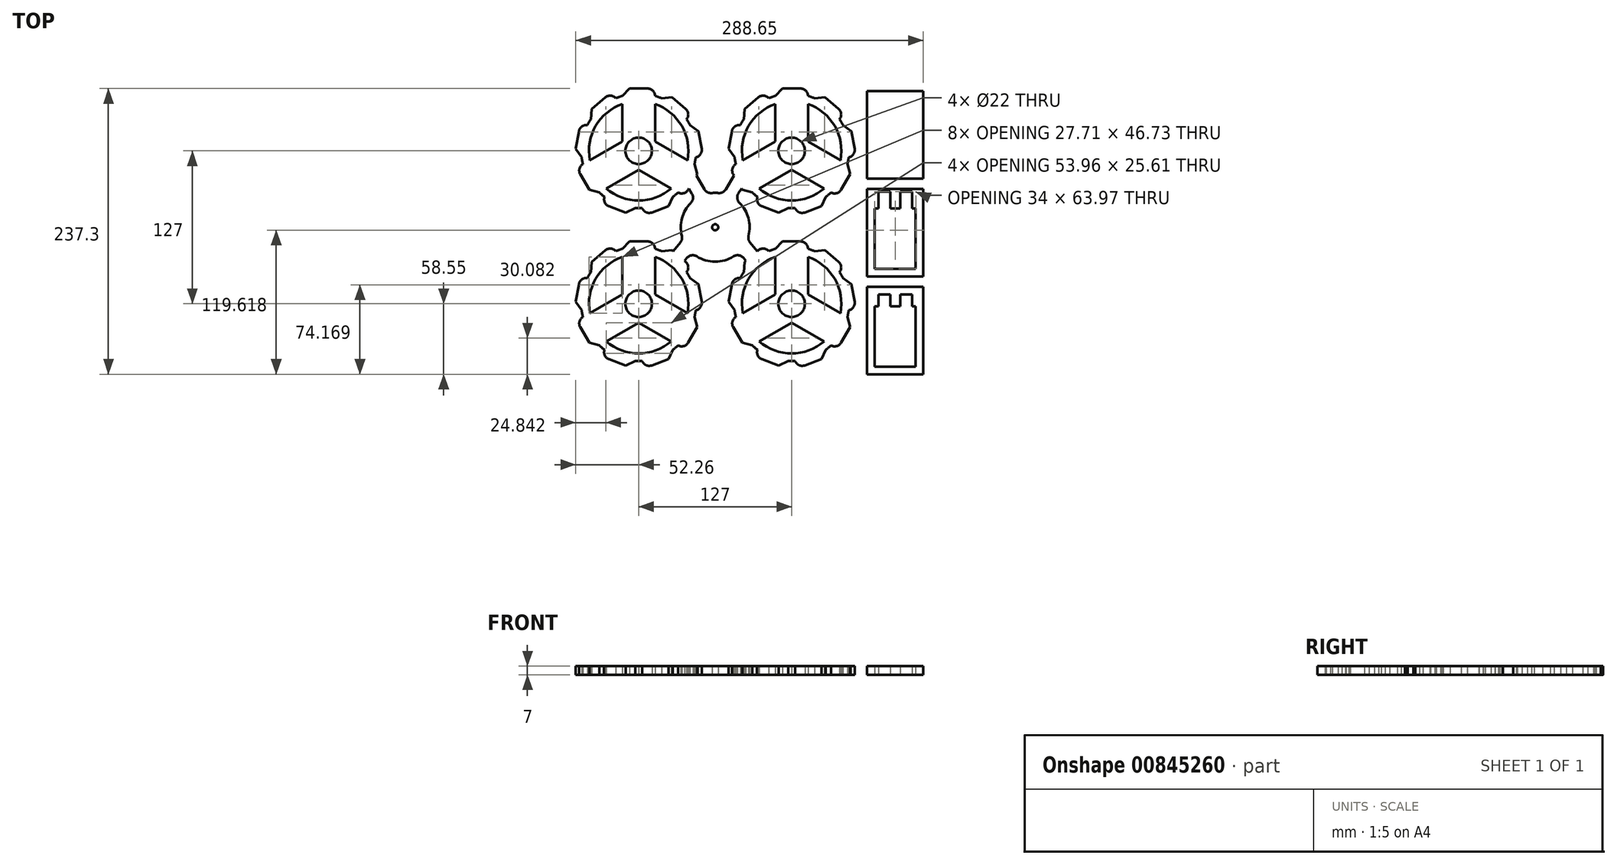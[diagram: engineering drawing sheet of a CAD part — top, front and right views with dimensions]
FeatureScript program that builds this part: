
annotation { "Feature Type Name" : "Feature", "Feature Type Description" : "" }
export const myFeature = defineFeature(function(context is Context, id is Id, definition is map)
    precondition{}
    {
        {
            var Q0;
            Q0=qCreatedBy(makeId("Top.planeOp"),FACE);
            var sketch = newSketch(context, id + "F0", { "sketchPlane" : qUnion([Q0])});
            skCircle(sketch, "E0", {"center": v(0, 0) * mm, "radius": 11 * mm});
            skCircle(sketch, "E1", {"center": v(0, 0) * mm, "radius": 13.56 * mm, "construction": true});
            skArc(sketch, "E2", {"start": v(-13.56, 38.98) * mm, "mid": v(0, -41.28) * mm, "end": v(13.56, 38.98) * mm});
            skArc(sketch, "E3", {"start": v(-13.56, 45.65) * mm, "mid": v(-16.29, 44.75) * mm, "end": v(-18.95, 43.7) * mm});
            skLineSegment(sketch, "E4.left", {"start": v(-13.56, 7.83) * mm, "end": v(-13.56, 38.98) * mm});
            skLineSegment(sketch, "E4.right", {"start": v(13.56, 7.83) * mm, "end": v(13.56, 38.98) * mm});
            skPoint(sketch, "E5.orphan", {"position": v(-13.56, 0) * mm});
            skLineSegment(sketch, "E6.top", {"start": v(-7.46, 51.75) * mm, "end": v(7.46, 51.75) * mm});
            skLineSegment(sketch, "E6.left", {"start": v(-13.56, 38.98) * mm, "end": v(-13.56, 45.65) * mm, "construction": true});
            skLineSegment(sketch, "E6.right", {"start": v(13.56, 38.98) * mm, "end": v(13.56, 45.65) * mm, "construction": true});
            skArc(sketch, "E7.filletArc", {"start": v(13.56, 45.65) * mm, "mid": v(11.78, 49.97) * mm, "end": v(7.46, 51.75) * mm});
            skLineSegment(sketch, "E8", {"start": v(-13.56, 45.65) * mm, "end": v(-7.46, 51.75) * mm});
            skLineSegment(sketch, "E9.1.0", {"start": v(-41.09, -32.34) * mm, "end": v(-48.55, -19.41) * mm});
            skLineSegment(sketch, "E9.1.1", {"start": v(-32.75, -34.57) * mm, "end": v(-41.09, -32.34) * mm});
            skLineSegment(sketch, "E9.1.2", {"start": v(-26.98, -31.24) * mm, "end": v(-32.75, -34.57) * mm, "construction": true});
            skLineSegment(sketch, "E9.1.3", {"start": v(0, -15.66) * mm, "end": v(-26.98, -31.24) * mm});
            skLineSegment(sketch, "E9.1.4", {"start": v(-13.56, 7.83) * mm, "end": v(-40.54, -7.74) * mm});
            skLineSegment(sketch, "E9.1.5", {"start": v(-40.54, -7.74) * mm, "end": v(-46.32, -11.08) * mm, "construction": true});
            skArc(sketch, "E9.1.6", {"start": v(-46.32, -11.08) * mm, "mid": v(-49.16, -14.78) * mm, "end": v(-48.55, -19.41) * mm});
            skLineSegment(sketch, "E9.2.0", {"start": v(48.55, -19.41) * mm, "end": v(47.92, -20.51) * mm});
            skLineSegment(sketch, "E9.2.1", {"start": v(46.32, -11.08) * mm, "end": v(48.55, -19.41) * mm});
            skLineSegment(sketch, "E9.2.2", {"start": v(40.54, -7.74) * mm, "end": v(46.32, -11.08) * mm, "construction": true});
            skLineSegment(sketch, "E9.2.3", {"start": v(13.56, 7.83) * mm, "end": v(40.54, -7.74) * mm});
            skLineSegment(sketch, "E9.2.4", {"start": v(0, -15.66) * mm, "end": v(26.98, -31.24) * mm});
            skLineSegment(sketch, "E9.2.5", {"start": v(26.98, -31.24) * mm, "end": v(32.75, -34.57) * mm, "construction": true});
            skArc(sketch, "E9.2.6", {"start": v(32.75, -34.57) * mm, "mid": v(37.38, -35.18) * mm, "end": v(41.09, -32.34) * mm});
            skPoint(sketch, "E10.orphan", {"position": v(-6.78, 11.75) * mm});
            skPoint(sketch, "E11.orphan", {"position": v(6.78, 11.75) * mm});
            skPoint(sketch, "E12.orphan", {"position": v(13.56, 0) * mm});
            skPoint(sketch, "E13.orphan", {"position": v(6.78, -11.75) * mm});
            skPoint(sketch, "E14.orphan", {"position": v(-6.78, -11.75) * mm});
            skLineSegment(sketch, "E15.1.0", {"start": v(-39.74, 26.25) * mm, "end": v(-38.98, 34.85) * mm});
            skLineSegment(sketch, "E15.1.1", {"start": v(-38.98, 34.85) * mm, "end": v(-27.55, 44.44) * mm});
            skArc(sketch, "E15.1.2", {"start": v(-18.95, 43.7) * mm, "mid": v(-23.1, 45.85) * mm, "end": v(-27.55, 44.44) * mm});
            skLineSegment(sketch, "E15.2.0", {"start": v(-47.31, -5.43) * mm, "end": v(-52.26, 1.64) * mm});
            skLineSegment(sketch, "E15.2.1", {"start": v(-52.26, 1.64) * mm, "end": v(-49.67, 16.34) * mm});
            skArc(sketch, "E15.2.2", {"start": v(-42.6, 21.29) * mm, "mid": v(-47.16, 20.27) * mm, "end": v(-49.67, 16.34) * mm});
            skLineSegment(sketch, "E15.4.0", {"start": v(-2.87, -47.54) * mm, "end": v(-10.69, -51.18) * mm});
            skLineSegment(sketch, "E15.4.1", {"start": v(-10.69, -51.18) * mm, "end": v(-24.71, -46.08) * mm});
            skArc(sketch, "E15.4.2", {"start": v(-28.36, -38.26) * mm, "mid": v(-28.16, -42.92) * mm, "end": v(-24.71, -46.08) * mm});
            skLineSegment(sketch, "E15.5.0", {"start": v(28.36, -38.26) * mm, "end": v(24.71, -46.08) * mm});
            skLineSegment(sketch, "E15.5.1", {"start": v(24.71, -46.08) * mm, "end": v(10.69, -51.18) * mm});
            skArc(sketch, "E15.5.2", {"start": v(2.87, -47.54) * mm, "mid": v(6.02, -50.98) * mm, "end": v(10.69, -51.18) * mm});
            skLineSegment(sketch, "E15.7.0", {"start": v(42.6, 21.29) * mm, "end": v(49.67, 16.34) * mm});
            skLineSegment(sketch, "E15.7.1", {"start": v(49.67, 16.34) * mm, "end": v(52.26, 1.64) * mm});
            skArc(sketch, "E15.7.2", {"start": v(47.31, -5.43) * mm, "mid": v(51.25, -2.92) * mm, "end": v(52.26, 1.64) * mm});
            skLineSegment(sketch, "E15.8.0", {"start": v(18.95, 43.7) * mm, "end": v(27.55, 44.44) * mm});
            skLineSegment(sketch, "E15.8.1", {"start": v(27.55, 44.44) * mm, "end": v(38.98, 34.85) * mm});
            skArc(sketch, "E15.8.2", {"start": v(39.74, 26.25) * mm, "mid": v(41.14, 30.7) * mm, "end": v(38.98, 34.85) * mm});
            skArc(sketch, "E16.trimOffspring", {"start": v(-39.74, 26.25) * mm, "mid": v(-41.24, 23.81) * mm, "end": v(-42.6, 21.29) * mm});
            skArc(sketch, "E17.trimOffspring", {"start": v(-47.31, -5.43) * mm, "mid": v(-46.9, -8.27) * mm, "end": v(-46.32, -11.08) * mm});
            skArc(sketch, "E18.trimOffspring", {"start": v(-32.75, -34.57) * mm, "mid": v(-30.61, -36.48) * mm, "end": v(-28.36, -38.26) * mm});
            skArc(sketch, "E19.trimOffspring", {"start": v(-2.87, -47.54) * mm, "mid": v(0, -47.63) * mm, "end": v(2.87, -47.54) * mm});
            skArc(sketch, "E20.trimOffspring", {"start": v(28.36, -38.26) * mm, "mid": v(30.61, -36.48) * mm, "end": v(32.75, -34.57) * mm});
            skArc(sketch, "E21.trimOffspring", {"start": v(46.32, -11.08) * mm, "mid": v(46.9, -8.27) * mm, "end": v(47.31, -5.43) * mm});
            skArc(sketch, "E22.trimOffspring", {"start": v(42.6, 21.29) * mm, "mid": v(41.24, 23.81) * mm, "end": v(39.74, 26.25) * mm});
            skArc(sketch, "E23.trimOffspring", {"start": v(18.95, 43.7) * mm, "mid": v(16.29, 44.75) * mm, "end": v(13.56, 45.65) * mm});
            skLineSegment(sketch, "E24.bottom", {"start": v(-58.61, -392.75) * mm, "end": v(550.99, -392.75) * mm, "construction": true});
            skLineSegment(sketch, "E24.top", {"start": v(-58.61, 64.45) * mm, "end": v(550.99, 64.45) * mm, "construction": true});
            skLineSegment(sketch, "E24.left", {"start": v(-58.61, -392.75) * mm, "end": v(-58.61, 64.45) * mm, "construction": true});
            skLineSegment(sketch, "E24.right", {"start": v(550.99, -392.75) * mm, "end": v(550.99, 64.45) * mm, "construction": true});
            skLineSegment(sketch, "E25.0.1.0", {"start": v(-26.98, -158.24) * mm, "end": v(-32.75, -161.57) * mm, "construction": true});
            skPoint(sketch, "E25.0.1.1", {"position": v(6.78, -115.25) * mm});
            skArc(sketch, "E25.0.1.2", {"start": v(-13.56, -81.35) * mm, "mid": v(-16.29, -82.25) * mm, "end": v(-18.95, -83.3) * mm});
            skArc(sketch, "E25.0.1.3", {"start": v(-42.6, -105.71) * mm, "mid": v(-47.16, -106.73) * mm, "end": v(-49.67, -110.66) * mm});
            skArc(sketch, "E25.0.1.4", {"start": v(46.32, -138.08) * mm, "mid": v(46.9, -135.27) * mm, "end": v(47.31, -132.43) * mm});
            skLineSegment(sketch, "E25.0.1.5", {"start": v(-2.87, -174.54) * mm, "end": v(-10.69, -178.18) * mm});
            skPoint(sketch, "E25.0.1.6", {"position": v(-13.56, -127) * mm});
            skArc(sketch, "E25.0.1.7", {"start": v(42.6, -105.71) * mm, "mid": v(41.24, -103.19) * mm, "end": v(39.74, -100.75) * mm});
            skPoint(sketch, "E25.0.1.8", {"position": v(-6.78, -115.25) * mm});
            skLineSegment(sketch, "E25.0.1.9", {"start": v(27.55, -82.56) * mm, "end": v(28.52, -83.37) * mm});
            skLineSegment(sketch, "E25.0.1.10", {"start": v(13.56, -88.02) * mm, "end": v(13.56, -81.35) * mm, "construction": true});
            skLineSegment(sketch, "E25.0.1.11", {"start": v(26.98, -158.24) * mm, "end": v(32.75, -161.57) * mm, "construction": true});
            skLineSegment(sketch, "E25.0.1.12", {"start": v(13.56, -119.17) * mm, "end": v(40.54, -134.74) * mm});
            skLineSegment(sketch, "E25.0.1.13", {"start": v(18.95, -83.3) * mm, "end": v(27.55, -82.56) * mm});
            skLineSegment(sketch, "E25.0.1.14", {"start": v(-13.56, -119.17) * mm, "end": v(-40.54, -134.74) * mm});
            skLineSegment(sketch, "E25.0.1.15", {"start": v(42.6, -105.71) * mm, "end": v(49.67, -110.66) * mm});
            skLineSegment(sketch, "E25.0.1.16", {"start": v(28.36, -165.26) * mm, "end": v(24.71, -173.08) * mm});
            skLineSegment(sketch, "E25.0.1.17", {"start": v(-13.56, -119.17) * mm, "end": v(-13.56, -88.02) * mm});
            skLineSegment(sketch, "E25.0.1.18", {"start": v(-38.98, -92.15) * mm, "end": v(-27.55, -82.56) * mm});
            skArc(sketch, "E25.0.1.19", {"start": v(28.36, -165.26) * mm, "mid": v(30.61, -163.48) * mm, "end": v(32.75, -161.57) * mm});
            skPoint(sketch, "E25.0.1.20", {"position": v(6.78, -138.75) * mm});
            skArc(sketch, "E25.0.1.21", {"start": v(47.31, -132.43) * mm, "mid": v(51.25, -129.92) * mm, "end": v(52.26, -125.36) * mm});
            skLineSegment(sketch, "E25.0.1.22", {"start": v(-41.09, -159.34) * mm, "end": v(-48.55, -146.41) * mm});
            skLineSegment(sketch, "E25.0.1.23", {"start": v(-39.74, -100.75) * mm, "end": v(-38.98, -92.15) * mm});
            skArc(sketch, "E25.0.1.24", {"start": v(2.87, -174.54) * mm, "mid": v(6.02, -177.98) * mm, "end": v(10.69, -178.18) * mm});
            skPoint(sketch, "E25.0.1.25", {"position": v(0, -127) * mm});
            skLineSegment(sketch, "E25.0.1.26", {"start": v(0, -142.66) * mm, "end": v(26.98, -158.24) * mm});
            skLineSegment(sketch, "E25.0.1.27", {"start": v(-47.31, -132.43) * mm, "end": v(-52.26, -125.36) * mm});
            skLineSegment(sketch, "E25.0.1.28", {"start": v(40.54, -134.74) * mm, "end": v(46.32, -138.08) * mm, "construction": true});
            skArc(sketch, "E25.0.1.29", {"start": v(-28.36, -165.26) * mm, "mid": v(-28.16, -169.92) * mm, "end": v(-24.71, -173.08) * mm});
            skPoint(sketch, "E25.0.1.30", {"position": v(-6.78, -138.75) * mm});
            skArc(sketch, "E25.0.1.31", {"start": v(39.74, -100.75) * mm, "mid": v(41.14, -96.3) * mm, "end": v(38.98, -92.15) * mm});
            skLineSegment(sketch, "E25.0.1.32", {"start": v(-7.46, -75.25) * mm, "end": v(7.46, -75.25) * mm});
            skLineSegment(sketch, "E25.0.1.33", {"start": v(0, -142.66) * mm, "end": v(-26.98, -158.24) * mm});
            skLineSegment(sketch, "E25.0.1.34", {"start": v(49.67, -110.66) * mm, "end": v(52.26, -125.36) * mm});
            skPoint(sketch, "E25.0.1.35", {"position": v(13.56, -127) * mm});
            skLineSegment(sketch, "E25.0.1.36", {"start": v(24.71, -173.08) * mm, "end": v(10.69, -178.18) * mm});
            skArc(sketch, "E25.0.1.37", {"start": v(18.95, -83.3) * mm, "mid": v(16.29, -82.25) * mm, "end": v(13.56, -81.35) * mm});
            skArc(sketch, "E25.0.1.38", {"start": v(-47.31, -132.43) * mm, "mid": v(-46.9, -135.27) * mm, "end": v(-46.32, -138.08) * mm});
            skCircle(sketch, "E25.0.1.39", {"center": v(0, -127) * mm, "radius": 13.56 * mm, "construction": true});
            skLineSegment(sketch, "E25.0.1.40", {"start": v(-32.75, -161.57) * mm, "end": v(-41.09, -159.34) * mm});
            skArc(sketch, "E25.0.1.41", {"start": v(32.75, -161.57) * mm, "mid": v(37.38, -162.18) * mm, "end": v(41.09, -159.34) * mm});
            skArc(sketch, "E25.0.1.42", {"start": v(-18.95, -83.3) * mm, "mid": v(-23.1, -81.15) * mm, "end": v(-27.55, -82.56) * mm});
            skArc(sketch, "E25.0.1.43", {"start": v(-13.56, -88.02) * mm, "mid": v(0, -168.28) * mm, "end": v(13.56, -88.02) * mm});
            skArc(sketch, "E25.0.1.44", {"start": v(-46.32, -138.08) * mm, "mid": v(-49.16, -141.78) * mm, "end": v(-48.55, -146.41) * mm});
            skLineSegment(sketch, "E25.0.1.45", {"start": v(-40.54, -134.74) * mm, "end": v(-46.32, -138.08) * mm, "construction": true});
            skArc(sketch, "E25.0.1.46", {"start": v(-39.74, -100.75) * mm, "mid": v(-41.24, -103.19) * mm, "end": v(-42.6, -105.71) * mm});
            skArc(sketch, "E25.0.1.47", {"start": v(13.56, -81.35) * mm, "mid": v(11.78, -77.03) * mm, "end": v(7.46, -75.25) * mm});
            skLineSegment(sketch, "E25.0.1.48", {"start": v(-10.69, -178.18) * mm, "end": v(-24.71, -173.08) * mm});
            skLineSegment(sketch, "E25.0.1.49", {"start": v(-13.56, -88.02) * mm, "end": v(-13.56, -81.35) * mm, "construction": true});
            skLineSegment(sketch, "E25.0.1.50", {"start": v(48.55, -146.41) * mm, "end": v(41.09, -159.34) * mm});
            skLineSegment(sketch, "E25.0.1.51", {"start": v(46.32, -138.08) * mm, "end": v(48.55, -146.41) * mm});
            skLineSegment(sketch, "E25.0.1.52", {"start": v(13.56, -119.17) * mm, "end": v(13.56, -88.02) * mm});
            skArc(sketch, "E25.0.1.53", {"start": v(-2.87, -174.54) * mm, "mid": v(0, -174.62) * mm, "end": v(2.87, -174.54) * mm});
            skLineSegment(sketch, "E25.0.1.54", {"start": v(-52.26, -125.36) * mm, "end": v(-49.67, -110.66) * mm});
            skCircle(sketch, "E25.0.1.55", {"center": v(0, -127) * mm, "radius": 11 * mm});
            skArc(sketch, "E25.0.1.56", {"start": v(-32.75, -161.57) * mm, "mid": v(-30.61, -163.48) * mm, "end": v(-28.36, -165.26) * mm});
            skArc(sketch, "E25.0.1.57", {"start": v(32.75, -161.57) * mm, "mid": v(37.38, -162.18) * mm, "end": v(41.09, -159.34) * mm});
            skLineSegment(sketch, "E25.0.1.58", {"start": v(48.55, -146.41) * mm, "end": v(41.09, -159.34) * mm});
            skArc(sketch, "E25.0.1.59", {"start": v(-46.32, -138.08) * mm, "mid": v(-49.16, -141.78) * mm, "end": v(-48.55, -146.41) * mm});
            skLineSegment(sketch, "E25.0.1.60", {"start": v(-13.56, -81.35) * mm, "end": v(-7.46, -75.25) * mm});
            skLineSegment(sketch, "E25.0.1.61", {"start": v(46.32, -138.08) * mm, "end": v(48.55, -146.41) * mm});
            skLineSegment(sketch, "E25.0.1.62", {"start": v(-32.75, -161.57) * mm, "end": v(-41.09, -159.34) * mm});
            skPoint(sketch, "E25.0.1.63", {"position": v(0, -127) * mm});
            skLineSegment(sketch, "E25.0.1.64", {"start": v(-41.09, -159.34) * mm, "end": v(-48.55, -146.41) * mm});
            skPoint(sketch, "E25.0.1.65", {"position": v(0, -127) * mm});
            skPoint(sketch, "E25.0.1.66", {"position": v(0, -127) * mm});
            skPoint(sketch, "E25.0.1.67", {"position": v(0, -127) * mm});
            skPoint(sketch, "E25.0.1.68", {"position": v(0, -127) * mm});
            skLineSegment(sketch, "E25.1.0.0", {"start": v(100.02, -31.24) * mm, "end": v(94.25, -34.57) * mm, "construction": true});
            skPoint(sketch, "E25.1.0.1", {"position": v(133.78, 11.75) * mm});
            skArc(sketch, "E25.1.0.2", {"start": v(113.44, 45.65) * mm, "mid": v(110.71, 44.75) * mm, "end": v(108.05, 43.7) * mm});
            skArc(sketch, "E25.1.0.3", {"start": v(84.4, 21.29) * mm, "mid": v(79.84, 20.27) * mm, "end": v(77.33, 16.34) * mm});
            skArc(sketch, "E25.1.0.4", {"start": v(173.32, -11.08) * mm, "mid": v(173.9, -8.27) * mm, "end": v(174.31, -5.43) * mm});
            skLineSegment(sketch, "E25.1.0.5", {"start": v(124.13, -47.54) * mm, "end": v(116.31, -51.18) * mm});
            skPoint(sketch, "E25.1.0.6", {"position": v(113.44, 0) * mm});
            skArc(sketch, "E25.1.0.7", {"start": v(169.6, 21.29) * mm, "mid": v(168.24, 23.81) * mm, "end": v(166.74, 26.25) * mm});
            skPoint(sketch, "E25.1.0.8", {"position": v(120.22, 11.75) * mm});
            skLineSegment(sketch, "E25.1.0.9", {"start": v(154.55, 44.44) * mm, "end": v(165.98, 34.85) * mm});
            skLineSegment(sketch, "E25.1.0.10", {"start": v(140.56, 38.98) * mm, "end": v(140.56, 45.65) * mm, "construction": true});
            skLineSegment(sketch, "E25.1.0.11", {"start": v(153.98, -31.24) * mm, "end": v(159.75, -34.57) * mm, "construction": true});
            skLineSegment(sketch, "E25.1.0.12", {"start": v(140.56, 7.83) * mm, "end": v(167.54, -7.74) * mm});
            skLineSegment(sketch, "E25.1.0.13", {"start": v(145.95, 43.7) * mm, "end": v(154.55, 44.44) * mm});
            skLineSegment(sketch, "E25.1.0.14", {"start": v(113.44, 7.83) * mm, "end": v(86.46, -7.74) * mm});
            skLineSegment(sketch, "E25.1.0.15", {"start": v(169.6, 21.29) * mm, "end": v(176.67, 16.34) * mm});
            skLineSegment(sketch, "E25.1.0.16", {"start": v(155.36, -38.26) * mm, "end": v(151.71, -46.08) * mm});
            skLineSegment(sketch, "E25.1.0.17", {"start": v(113.44, 7.83) * mm, "end": v(113.44, 38.98) * mm});
            skLineSegment(sketch, "E25.1.0.18", {"start": v(88.02, 34.85) * mm, "end": v(99.45, 44.44) * mm});
            skArc(sketch, "E25.1.0.19", {"start": v(155.36, -38.26) * mm, "mid": v(157.61, -36.48) * mm, "end": v(159.75, -34.57) * mm});
            skPoint(sketch, "E25.1.0.20", {"position": v(133.78, -11.75) * mm});
            skArc(sketch, "E25.1.0.21", {"start": v(174.31, -5.43) * mm, "mid": v(178.25, -2.92) * mm, "end": v(179.26, 1.64) * mm});
            skLineSegment(sketch, "E25.1.0.22", {"start": v(85.91, -32.34) * mm, "end": v(85.28, -31.24) * mm});
            skLineSegment(sketch, "E25.1.0.23", {"start": v(87.26, 26.25) * mm, "end": v(88.02, 34.85) * mm});
            skArc(sketch, "E25.1.0.24", {"start": v(129.87, -47.54) * mm, "mid": v(133.02, -50.98) * mm, "end": v(137.69, -51.18) * mm});
            skPoint(sketch, "E25.1.0.25", {"position": v(127, 0) * mm});
            skLineSegment(sketch, "E25.1.0.26", {"start": v(127, -15.66) * mm, "end": v(153.98, -31.24) * mm});
            skLineSegment(sketch, "E25.1.0.27", {"start": v(79.69, -5.43) * mm, "end": v(74.74, 1.64) * mm});
            skLineSegment(sketch, "E25.1.0.28", {"start": v(167.54, -7.74) * mm, "end": v(173.32, -11.08) * mm, "construction": true});
            skArc(sketch, "E25.1.0.29", {"start": v(98.64, -38.26) * mm, "mid": v(98.84, -42.92) * mm, "end": v(102.29, -46.08) * mm});
            skPoint(sketch, "E25.1.0.30", {"position": v(120.22, -11.75) * mm});
            skArc(sketch, "E25.1.0.31", {"start": v(166.74, 26.25) * mm, "mid": v(168.14, 30.7) * mm, "end": v(165.98, 34.85) * mm});
            skLineSegment(sketch, "E25.1.0.32", {"start": v(119.54, 51.75) * mm, "end": v(134.46, 51.75) * mm});
            skLineSegment(sketch, "E25.1.0.33", {"start": v(127, -15.66) * mm, "end": v(100.02, -31.24) * mm});
            skLineSegment(sketch, "E25.1.0.34", {"start": v(176.67, 16.34) * mm, "end": v(179.26, 1.64) * mm});
            skPoint(sketch, "E25.1.0.35", {"position": v(140.56, 0) * mm});
            skLineSegment(sketch, "E25.1.0.36", {"start": v(151.71, -46.08) * mm, "end": v(137.69, -51.18) * mm});
            skArc(sketch, "E25.1.0.37", {"start": v(145.95, 43.7) * mm, "mid": v(143.29, 44.75) * mm, "end": v(140.56, 45.65) * mm});
            skArc(sketch, "E25.1.0.38", {"start": v(79.69, -5.43) * mm, "mid": v(80.1, -8.27) * mm, "end": v(80.68, -11.08) * mm});
            skCircle(sketch, "E25.1.0.39", {"center": v(127, 0) * mm, "radius": 13.56 * mm, "construction": true});
            skLineSegment(sketch, "E25.1.0.40", {"start": v(94.25, -34.57) * mm, "end": v(85.91, -32.34) * mm});
            skArc(sketch, "E25.1.0.41", {"start": v(159.75, -34.57) * mm, "mid": v(164.38, -35.18) * mm, "end": v(168.09, -32.34) * mm});
            skArc(sketch, "E25.1.0.42", {"start": v(108.05, 43.7) * mm, "mid": v(103.9, 45.85) * mm, "end": v(99.45, 44.44) * mm});
            skArc(sketch, "E25.1.0.43", {"start": v(113.44, 38.98) * mm, "mid": v(127, -41.28) * mm, "end": v(140.56, 38.98) * mm});
            skArc(sketch, "E25.1.0.44", {"start": v(80.68, -11.08) * mm, "mid": v(77.84, -14.78) * mm, "end": v(78.45, -19.41) * mm});
            skLineSegment(sketch, "E25.1.0.45", {"start": v(86.46, -7.74) * mm, "end": v(80.68, -11.08) * mm, "construction": true});
            skArc(sketch, "E25.1.0.46", {"start": v(87.26, 26.25) * mm, "mid": v(85.76, 23.81) * mm, "end": v(84.4, 21.29) * mm});
            skArc(sketch, "E25.1.0.47", {"start": v(140.56, 45.65) * mm, "mid": v(138.78, 49.97) * mm, "end": v(134.46, 51.75) * mm});
            skLineSegment(sketch, "E25.1.0.48", {"start": v(116.31, -51.18) * mm, "end": v(102.29, -46.08) * mm});
            skLineSegment(sketch, "E25.1.0.49", {"start": v(113.44, 38.98) * mm, "end": v(113.44, 45.65) * mm, "construction": true});
            skLineSegment(sketch, "E25.1.0.50", {"start": v(175.55, -19.41) * mm, "end": v(168.09, -32.34) * mm});
            skLineSegment(sketch, "E25.1.0.51", {"start": v(173.32, -11.08) * mm, "end": v(175.55, -19.41) * mm});
            skLineSegment(sketch, "E25.1.0.52", {"start": v(140.56, 7.83) * mm, "end": v(140.56, 38.98) * mm});
            skArc(sketch, "E25.1.0.53", {"start": v(124.13, -47.54) * mm, "mid": v(127, -47.62) * mm, "end": v(129.87, -47.54) * mm});
            skLineSegment(sketch, "E25.1.0.54", {"start": v(74.74, 1.64) * mm, "end": v(77.33, 16.34) * mm});
            skCircle(sketch, "E25.1.0.55", {"center": v(127, 0) * mm, "radius": 11 * mm});
            skArc(sketch, "E25.1.0.56", {"start": v(94.25, -34.57) * mm, "mid": v(96.39, -36.48) * mm, "end": v(98.64, -38.26) * mm});
            skArc(sketch, "E25.1.0.57", {"start": v(159.75, -34.57) * mm, "mid": v(164.38, -35.18) * mm, "end": v(168.09, -32.34) * mm});
            skLineSegment(sketch, "E25.1.0.58", {"start": v(175.55, -19.41) * mm, "end": v(168.09, -32.34) * mm});
            skArc(sketch, "E25.1.0.59", {"start": v(80.68, -11.08) * mm, "mid": v(77.84, -14.78) * mm, "end": v(78.45, -19.41) * mm});
            skLineSegment(sketch, "E25.1.0.60", {"start": v(113.44, 45.65) * mm, "end": v(119.54, 51.75) * mm});
            skLineSegment(sketch, "E25.1.0.61", {"start": v(173.32, -11.08) * mm, "end": v(175.55, -19.41) * mm});
            skLineSegment(sketch, "E25.1.0.62", {"start": v(94.25, -34.57) * mm, "end": v(85.91, -32.34) * mm});
            skPoint(sketch, "E25.1.0.63", {"position": v(127, 0) * mm});
            skLineSegment(sketch, "E25.1.0.64", {"start": v(85.91, -32.34) * mm, "end": v(85.28, -31.24) * mm});
            skPoint(sketch, "E25.1.0.65", {"position": v(127, 0) * mm});
            skPoint(sketch, "E25.1.0.66", {"position": v(127, 0) * mm});
            skPoint(sketch, "E25.1.0.67", {"position": v(127, 0) * mm});
            skPoint(sketch, "E25.1.0.68", {"position": v(127, 0) * mm});
            skLineSegment(sketch, "E25.1.1.0", {"start": v(100.02, -158.24) * mm, "end": v(94.25, -161.57) * mm, "construction": true});
            skPoint(sketch, "E25.1.1.1", {"position": v(133.78, -115.25) * mm});
            skArc(sketch, "E25.1.1.2", {"start": v(113.44, -81.35) * mm, "mid": v(110.71, -82.25) * mm, "end": v(108.05, -83.3) * mm});
            skArc(sketch, "E25.1.1.3", {"start": v(84.4, -105.71) * mm, "mid": v(79.84, -106.73) * mm, "end": v(77.33, -110.66) * mm});
            skArc(sketch, "E25.1.1.4", {"start": v(173.32, -138.08) * mm, "mid": v(173.9, -135.27) * mm, "end": v(174.31, -132.43) * mm});
            skLineSegment(sketch, "E25.1.1.5", {"start": v(124.13, -174.54) * mm, "end": v(116.31, -178.18) * mm});
            skPoint(sketch, "E25.1.1.6", {"position": v(113.44, -127) * mm});
            skArc(sketch, "E25.1.1.7", {"start": v(169.6, -105.71) * mm, "mid": v(168.24, -103.19) * mm, "end": v(166.74, -100.75) * mm});
            skPoint(sketch, "E25.1.1.8", {"position": v(120.22, -115.25) * mm});
            skLineSegment(sketch, "E25.1.1.9", {"start": v(154.55, -82.56) * mm, "end": v(165.98, -92.15) * mm});
            skLineSegment(sketch, "E25.1.1.10", {"start": v(140.56, -88.02) * mm, "end": v(140.56, -81.35) * mm, "construction": true});
            skLineSegment(sketch, "E25.1.1.11", {"start": v(153.98, -158.24) * mm, "end": v(159.75, -161.57) * mm, "construction": true});
            skLineSegment(sketch, "E25.1.1.12", {"start": v(140.56, -119.17) * mm, "end": v(167.54, -134.74) * mm});
            skLineSegment(sketch, "E25.1.1.13", {"start": v(145.95, -83.3) * mm, "end": v(154.55, -82.56) * mm});
            skLineSegment(sketch, "E25.1.1.14", {"start": v(113.44, -119.17) * mm, "end": v(86.46, -134.74) * mm});
            skLineSegment(sketch, "E25.1.1.15", {"start": v(169.6, -105.71) * mm, "end": v(176.67, -110.66) * mm});
            skLineSegment(sketch, "E25.1.1.16", {"start": v(155.36, -165.26) * mm, "end": v(151.71, -173.08) * mm});
            skLineSegment(sketch, "E25.1.1.17", {"start": v(113.44, -119.17) * mm, "end": v(113.44, -88.02) * mm});
            skLineSegment(sketch, "E25.1.1.18", {"start": v(88.02, -92.15) * mm, "end": v(88.99, -91.34) * mm});
            skArc(sketch, "E25.1.1.19", {"start": v(155.36, -165.26) * mm, "mid": v(157.61, -163.48) * mm, "end": v(159.75, -161.57) * mm});
            skPoint(sketch, "E25.1.1.20", {"position": v(133.78, -138.75) * mm});
            skArc(sketch, "E25.1.1.21", {"start": v(174.31, -132.43) * mm, "mid": v(178.25, -129.92) * mm, "end": v(179.26, -125.36) * mm});
            skLineSegment(sketch, "E25.1.1.22", {"start": v(85.91, -159.34) * mm, "end": v(78.45, -146.41) * mm});
            skLineSegment(sketch, "E25.1.1.23", {"start": v(87.26, -100.75) * mm, "end": v(88.02, -92.15) * mm});
            skArc(sketch, "E25.1.1.24", {"start": v(129.87, -174.54) * mm, "mid": v(133.02, -177.98) * mm, "end": v(137.69, -178.18) * mm});
            skPoint(sketch, "E25.1.1.25", {"position": v(127, -127) * mm});
            skLineSegment(sketch, "E25.1.1.26", {"start": v(127, -142.66) * mm, "end": v(153.98, -158.24) * mm});
            skLineSegment(sketch, "E25.1.1.27", {"start": v(79.69, -132.43) * mm, "end": v(74.74, -125.36) * mm});
            skLineSegment(sketch, "E25.1.1.28", {"start": v(167.54, -134.74) * mm, "end": v(173.32, -138.08) * mm, "construction": true});
            skArc(sketch, "E25.1.1.29", {"start": v(98.64, -165.26) * mm, "mid": v(98.84, -169.92) * mm, "end": v(102.29, -173.08) * mm});
            skPoint(sketch, "E25.1.1.30", {"position": v(120.22, -138.75) * mm});
            skArc(sketch, "E25.1.1.31", {"start": v(166.74, -100.75) * mm, "mid": v(168.14, -96.3) * mm, "end": v(165.98, -92.15) * mm});
            skLineSegment(sketch, "E25.1.1.32", {"start": v(119.54, -75.25) * mm, "end": v(134.46, -75.25) * mm});
            skLineSegment(sketch, "E25.1.1.33", {"start": v(127, -142.66) * mm, "end": v(100.02, -158.24) * mm});
            skLineSegment(sketch, "E25.1.1.34", {"start": v(176.67, -110.66) * mm, "end": v(179.26, -125.36) * mm});
            skPoint(sketch, "E25.1.1.35", {"position": v(140.56, -127) * mm});
            skLineSegment(sketch, "E25.1.1.36", {"start": v(151.71, -173.08) * mm, "end": v(137.69, -178.18) * mm});
            skArc(sketch, "E25.1.1.37", {"start": v(145.95, -83.3) * mm, "mid": v(143.29, -82.25) * mm, "end": v(140.56, -81.35) * mm});
            skArc(sketch, "E25.1.1.38", {"start": v(79.69, -132.43) * mm, "mid": v(80.1, -135.27) * mm, "end": v(80.68, -138.08) * mm});
            skCircle(sketch, "E25.1.1.39", {"center": v(127, -127) * mm, "radius": 13.56 * mm, "construction": true});
            skLineSegment(sketch, "E25.1.1.40", {"start": v(94.25, -161.57) * mm, "end": v(85.91, -159.34) * mm});
            skArc(sketch, "E25.1.1.41", {"start": v(159.75, -161.57) * mm, "mid": v(164.38, -162.18) * mm, "end": v(168.09, -159.34) * mm});
            skArc(sketch, "E25.1.1.42", {"start": v(108.05, -83.3) * mm, "mid": v(103.9, -81.15) * mm, "end": v(99.45, -82.56) * mm});
            skArc(sketch, "E25.1.1.43", {"start": v(113.44, -88.02) * mm, "mid": v(127, -168.28) * mm, "end": v(140.56, -88.02) * mm});
            skArc(sketch, "E25.1.1.44", {"start": v(80.68, -138.08) * mm, "mid": v(77.84, -141.78) * mm, "end": v(78.45, -146.41) * mm});
            skLineSegment(sketch, "E25.1.1.45", {"start": v(86.46, -134.74) * mm, "end": v(80.68, -138.08) * mm, "construction": true});
            skArc(sketch, "E25.1.1.46", {"start": v(87.26, -100.75) * mm, "mid": v(85.76, -103.19) * mm, "end": v(84.4, -105.71) * mm});
            skArc(sketch, "E25.1.1.47", {"start": v(140.56, -81.35) * mm, "mid": v(138.78, -77.03) * mm, "end": v(134.46, -75.25) * mm});
            skLineSegment(sketch, "E25.1.1.48", {"start": v(116.31, -178.18) * mm, "end": v(102.29, -173.08) * mm});
            skLineSegment(sketch, "E25.1.1.49", {"start": v(113.44, -88.02) * mm, "end": v(113.44, -81.35) * mm, "construction": true});
            skLineSegment(sketch, "E25.1.1.50", {"start": v(175.55, -146.41) * mm, "end": v(168.09, -159.34) * mm});
            skLineSegment(sketch, "E25.1.1.51", {"start": v(173.32, -138.08) * mm, "end": v(175.55, -146.41) * mm});
            skLineSegment(sketch, "E25.1.1.52", {"start": v(140.56, -119.17) * mm, "end": v(140.56, -88.02) * mm});
            skArc(sketch, "E25.1.1.53", {"start": v(124.13, -174.54) * mm, "mid": v(127, -174.62) * mm, "end": v(129.87, -174.54) * mm});
            skLineSegment(sketch, "E25.1.1.54", {"start": v(74.74, -125.36) * mm, "end": v(77.33, -110.66) * mm});
            skCircle(sketch, "E25.1.1.55", {"center": v(127, -127) * mm, "radius": 11 * mm});
            skArc(sketch, "E25.1.1.56", {"start": v(94.25, -161.57) * mm, "mid": v(96.39, -163.48) * mm, "end": v(98.64, -165.26) * mm});
            skArc(sketch, "E25.1.1.57", {"start": v(159.75, -161.57) * mm, "mid": v(164.38, -162.18) * mm, "end": v(168.09, -159.34) * mm});
            skLineSegment(sketch, "E25.1.1.58", {"start": v(175.55, -146.41) * mm, "end": v(168.09, -159.34) * mm});
            skArc(sketch, "E25.1.1.59", {"start": v(80.68, -138.08) * mm, "mid": v(77.84, -141.78) * mm, "end": v(78.45, -146.41) * mm});
            skLineSegment(sketch, "E25.1.1.60", {"start": v(113.44, -81.35) * mm, "end": v(119.54, -75.25) * mm});
            skLineSegment(sketch, "E25.1.1.61", {"start": v(173.32, -138.08) * mm, "end": v(175.55, -146.41) * mm});
            skLineSegment(sketch, "E25.1.1.62", {"start": v(94.25, -161.57) * mm, "end": v(85.91, -159.34) * mm});
            skPoint(sketch, "E25.1.1.63", {"position": v(127, -127) * mm});
            skLineSegment(sketch, "E25.1.1.64", {"start": v(85.91, -159.34) * mm, "end": v(78.45, -146.41) * mm});
            skPoint(sketch, "E25.1.1.65", {"position": v(127, -127) * mm});
            skPoint(sketch, "E25.1.1.66", {"position": v(127, -127) * mm});
            skPoint(sketch, "E25.1.1.67", {"position": v(127, -127) * mm});
            skPoint(sketch, "E25.1.1.68", {"position": v(127, -127) * mm});
            skLineSegment(sketch, "E25.direction1", {"start": v(-41.09, -32.34) * mm, "end": v(85.91, -32.34) * mm, "construction": true});
            skLineSegment(sketch, "E25.direction2", {"start": v(-41.09, -32.34) * mm, "end": v(-41.09, -159.34) * mm, "construction": true});
            skLineSegment(sketch, "E26.bottom", {"start": v(-58.61, 64.45) * mm, "end": v(236.39, 64.45) * mm, "construction": true});
            skLineSegment(sketch, "E26.top", {"start": v(-58.61, -185.55) * mm, "end": v(236.39, -185.55) * mm, "construction": true});
            skLineSegment(sketch, "E26.left", {"start": v(-58.61, 64.45) * mm, "end": v(-58.61, -185.55) * mm, "construction": true});
            skLineSegment(sketch, "E26.right", {"start": v(236.39, 64.45) * mm, "end": v(236.39, -185.55) * mm, "construction": true});
            skLineSegment(sketch, "E27.bottom", {"start": v(0, 0) * mm, "end": v(127, 0) * mm, "construction": true});
            skLineSegment(sketch, "E27.top", {"start": v(0, -127) * mm, "end": v(127, -127) * mm, "construction": true});
            skLineSegment(sketch, "E27.left", {"start": v(0, 0) * mm, "end": v(0, -127) * mm, "construction": true});
            skLineSegment(sketch, "E27.right", {"start": v(127, 0) * mm, "end": v(127, -127) * mm, "construction": true});
            skArc(sketch, "E28", {"start": v(43.27, -43.32) * mm, "mid": v(35.94, -55.96) * mm, "end": v(35.81, -70.57) * mm});
            skPoint(sketch, "E28.centerSnap0", {"position": v(127, -63.5) * mm});
            skPoint(sketch, "E28.centerSnap1", {"position": v(63.5, -127) * mm});
            skLineSegment(sketch, "E29", {"start": v(47.92, -20.51) * mm, "end": v(54.5, -31.93) * mm});
            skLineSegment(sketch, "E30", {"start": v(41.72, -31.24) * mm, "end": v(44.27, -35.66) * mm});
            skLineSegment(sketch, "E31.trimOffspring", {"start": v(41.72, -31.24) * mm, "end": v(41.09, -32.34) * mm});
            skLineSegment(sketch, "E32", {"start": v(47.92, -20.51) * mm, "end": v(41.72, -31.24) * mm, "construction": true});
            skPoint(sketch, "E33.endSnap0", {"position": v(41.24, -103.19) * mm});
            skLineSegment(sketch, "E34", {"start": v(87, -88.96) * mm, "end": v(88.99, -91.34) * mm});
            skLineSegment(sketch, "E35", {"start": v(92.48, -76.22) * mm, "end": v(98.48, -83.37) * mm});
            skLineSegment(sketch, "E36", {"start": v(72.35, -31.96) * mm, "end": v(79.08, -20.51) * mm});
            skLineSegment(sketch, "E37", {"start": v(82.72, -35.58) * mm, "end": v(85.28, -31.24) * mm});
            skCircle(sketch, "E38", {"center": v(63.5, -63.5) * mm, "radius": 2.55 * mm});
            skLineSegment(sketch, "E39", {"start": v(28.52, -83.37) * mm, "end": v(34.52, -76.22) * mm});
            skLineSegment(sketch, "E40", {"start": v(38.01, -91.34) * mm, "end": v(40, -88.96) * mm});
            skArc(sketch, "E41.trimOffspring", {"start": v(66.26, -35.06) * mm, "mid": v(63.45, -34.93) * mm, "end": v(60.64, -35.07) * mm});
            skLineSegment(sketch, "E42.trimOffspring", {"start": v(79.08, -20.51) * mm, "end": v(78.45, -19.41) * mm});
            skLineSegment(sketch, "E43.trimOffspring", {"start": v(38.01, -91.34) * mm, "end": v(38.98, -92.15) * mm});
            skArc(sketch, "E44.trimOffspring", {"start": v(48.26, -87.67) * mm, "mid": v(63.5, -92.08) * mm, "end": v(78.74, -87.67) * mm});
            skArc(sketch, "E45.trimOffspring", {"start": v(91.19, -70.57) * mm, "mid": v(91.06, -55.94) * mm, "end": v(83.7, -43.3) * mm});
            skLineSegment(sketch, "E46.trimOffspring", {"start": v(98.48, -83.37) * mm, "end": v(99.45, -82.56) * mm});
            skPoint(sketch, "E47.visualSharp", {"position": v(56.7, -35.74) * mm});
            skArc(sketch, "E47.filletArc", {"start": v(54.5, -31.93) * mm, "mid": v(57.1, -34.4) * mm, "end": v(60.64, -35.07) * mm});
            skPoint(sketch, "E48.visualSharp", {"position": v(46.91, -40.23) * mm});
            skArc(sketch, "E48.filletArc", {"start": v(43.27, -43.32) * mm, "mid": v(45.07, -39.66) * mm, "end": v(44.27, -35.66) * mm});
            skPoint(sketch, "E49.visualSharp", {"position": v(70.14, -35.7) * mm});
            skArc(sketch, "E49.filletArc", {"start": v(66.26, -35.06) * mm, "mid": v(69.76, -34.4) * mm, "end": v(72.35, -31.96) * mm});
            skPoint(sketch, "E50.visualSharp", {"position": v(80.02, -40.18) * mm});
            skArc(sketch, "E50.filletArc", {"start": v(82.72, -35.58) * mm, "mid": v(81.9, -39.6) * mm, "end": v(83.7, -43.3) * mm});
            skPoint(sketch, "E51.visualSharp", {"position": v(36.75, -73.56) * mm});
            skArc(sketch, "E51.filletArc", {"start": v(34.52, -76.22) * mm, "mid": v(35.85, -73.55) * mm, "end": v(35.81, -70.57) * mm});
            skPoint(sketch, "E52.visualSharp", {"position": v(43.91, -84.3) * mm});
            skArc(sketch, "E52.filletArc", {"start": v(48.26, -87.67) * mm, "mid": v(43.89, -86.77) * mm, "end": v(40, -88.96) * mm});
            skPoint(sketch, "E53.visualSharp", {"position": v(83.09, -84.3) * mm});
            skArc(sketch, "E53.filletArc", {"start": v(87, -88.96) * mm, "mid": v(83.11, -86.77) * mm, "end": v(78.74, -87.67) * mm});
            skPoint(sketch, "E54.visualSharp", {"position": v(90.25, -73.56) * mm});
            skArc(sketch, "E54.filletArc", {"start": v(91.19, -70.57) * mm, "mid": v(91.15, -73.55) * mm, "end": v(92.48, -76.22) * mm});
            skLineSegment(sketch, "E55.8", {"start": v(227.04, -129.2) * mm, "end": v(227.04, -119.2) * mm});
            skLineSegment(sketch, "E55.9", {"start": v(227.04, -119.2) * mm, "end": v(217.04, -119.2) * mm});
            skLineSegment(sketch, "E55.10", {"start": v(217.04, -129.2) * mm, "end": v(217.04, -119.2) * mm});
            skLineSegment(sketch, "E55.11", {"start": v(196.04, -129.2) * mm, "end": v(199.04, -129.2) * mm});
            skLineSegment(sketch, "E55.13", {"start": v(230.04, -179.2) * mm, "end": v(230.04, -129.2) * mm});
            skLineSegment(sketch, "E55.14", {"start": v(196.04, -179.2) * mm, "end": v(230.04, -179.2) * mm});
            skLineSegment(sketch, "E55.15", {"start": v(196.04, -179.2) * mm, "end": v(196.04, -129.2) * mm});
            skLineSegment(sketch, "E56", {"start": v(227.04, -129.2) * mm, "end": v(230.04, -129.2) * mm});
            skLineSegment(sketch, "E57.top", {"start": v(199.04, -119.2) * mm, "end": v(209.04, -119.2) * mm});
            skLineSegment(sketch, "E57.left", {"start": v(199.04, -129.2) * mm, "end": v(199.04, -119.2) * mm});
            skLineSegment(sketch, "E57.right", {"start": v(209.04, -129.2) * mm, "end": v(209.04, -119.2) * mm});
            skLineSegment(sketch, "E58.trimOffspring", {"start": v(209.04, -129.2) * mm, "end": v(217.04, -129.2) * mm});
            skLineSegment(sketch, "E59.bottom", {"start": v(236.39, -185.55) * mm, "end": v(189.69, -185.55) * mm});
            skLineSegment(sketch, "E59.top", {"start": v(236.39, -112.85) * mm, "end": v(189.69, -112.85) * mm});
            skLineSegment(sketch, "E59.left", {"start": v(236.39, -185.55) * mm, "end": v(236.39, -112.85) * mm});
            skLineSegment(sketch, "E59.right", {"start": v(189.69, -185.55) * mm, "end": v(189.69, -112.85) * mm});
            skLineSegment(sketch, "E60.0.1.0", {"start": v(236.39, -31.57) * mm, "end": v(189.69, -31.57) * mm});
            skLineSegment(sketch, "E60.0.1.1", {"start": v(189.69, -104.27) * mm, "end": v(189.69, -31.57) * mm});
            skLineSegment(sketch, "E60.0.1.2", {"start": v(236.39, -104.27) * mm, "end": v(189.69, -104.27) * mm});
            skLineSegment(sketch, "E60.0.1.3", {"start": v(236.39, -104.27) * mm, "end": v(236.39, -31.57) * mm});
            skLineSegment(sketch, "E60.0.1.4", {"start": v(196.04, -97.92) * mm, "end": v(230.04, -97.92) * mm});
            skLineSegment(sketch, "E60.0.1.5", {"start": v(196.04, -97.92) * mm, "end": v(196.04, -47.92) * mm});
            skLineSegment(sketch, "E60.0.1.6", {"start": v(196.04, -47.92) * mm, "end": v(199.04, -47.92) * mm});
            skLineSegment(sketch, "E60.0.1.7", {"start": v(199.04, -47.92) * mm, "end": v(199.04, -37.92) * mm});
            skLineSegment(sketch, "E60.0.1.9", {"start": v(209.04, -47.92) * mm, "end": v(209.04, -37.92) * mm});
            skLineSegment(sketch, "E60.0.1.10", {"start": v(209.04, -47.92) * mm, "end": v(217.04, -47.92) * mm});
            skLineSegment(sketch, "E60.0.1.11", {"start": v(217.04, -47.92) * mm, "end": v(217.04, -37.92) * mm});
            skLineSegment(sketch, "E60.0.1.12", {"start": v(227.04, -37.92) * mm, "end": v(227.02, -37.92) * mm});
            skLineSegment(sketch, "E60.0.1.13", {"start": v(227.04, -47.92) * mm, "end": v(227.04, -37.92) * mm});
            skLineSegment(sketch, "E60.0.1.14", {"start": v(227.04, -47.92) * mm, "end": v(230.04, -47.92) * mm});
            skLineSegment(sketch, "E60.0.1.15", {"start": v(230.04, -97.92) * mm, "end": v(230.04, -47.92) * mm});
            skLineSegment(sketch, "E60.0.2.0", {"start": v(236.39, 49.71) * mm, "end": v(189.69, 49.71) * mm});
            skLineSegment(sketch, "E60.0.2.1", {"start": v(189.69, -22.99) * mm, "end": v(189.69, 49.71) * mm});
            skLineSegment(sketch, "E60.0.2.2", {"start": v(236.39, -22.99) * mm, "end": v(189.69, -22.99) * mm});
            skLineSegment(sketch, "E60.0.2.3", {"start": v(236.39, -22.99) * mm, "end": v(236.39, 49.71) * mm});
            skLineSegment(sketch, "E60.0.2.4", {"start": v(196.04, -16.64) * mm, "end": v(230.04, -16.64) * mm});
            skLineSegment(sketch, "E60.0.2.5", {"start": v(196.04, -16.64) * mm, "end": v(196.04, 33.36) * mm});
            skLineSegment(sketch, "E60.0.2.6", {"start": v(196.04, 33.36) * mm, "end": v(199.04, 33.36) * mm});
            skLineSegment(sketch, "E60.0.2.7", {"start": v(199.04, 33.36) * mm, "end": v(199.04, 43.36) * mm});
            skLineSegment(sketch, "E60.0.2.9", {"start": v(209.04, 33.36) * mm, "end": v(209.04, 43.36) * mm});
            skLineSegment(sketch, "E60.0.2.10", {"start": v(209.04, 33.36) * mm, "end": v(217.04, 33.36) * mm});
            skLineSegment(sketch, "E60.0.2.11", {"start": v(217.04, 33.36) * mm, "end": v(217.04, 43.36) * mm});
            skLineSegment(sketch, "E60.0.2.13", {"start": v(227.04, 33.36) * mm, "end": v(227.04, 43.36) * mm});
            skLineSegment(sketch, "E60.0.2.14", {"start": v(227.04, 33.36) * mm, "end": v(230.04, 33.36) * mm});
            skLineSegment(sketch, "E60.0.2.15", {"start": v(230.04, -16.64) * mm, "end": v(230.04, 33.36) * mm});
            skLineSegment(sketch, "E60.direction1", {"start": v(189.69, -112.85) * mm, "end": v(215.09, -112.85) * mm, "construction": true});
            skLineSegment(sketch, "E60.direction2", {"start": v(189.69, -112.85) * mm, "end": v(189.69, -31.57) * mm, "construction": true});
            skLineSegment(sketch, "E61.left", {"start": v(199.04, 43.36) * mm, "end": v(199.04, 49.71) * mm});
            skLineSegment(sketch, "E61.right", {"start": v(209.04, 43.36) * mm, "end": v(209.04, 49.71) * mm});
            skLineSegment(sketch, "E62.bottom", {"start": v(227.04, 43.36) * mm, "end": v(227.28, 43.36) * mm});
            skLineSegment(sketch, "E62.left", {"start": v(217.04, 43.36) * mm, "end": v(217.04, 49.71) * mm});
            skLineSegment(sketch, "E62.right", {"start": v(227.28, 43.36) * mm, "end": v(227.28, 49.71) * mm});
            skPoint(sketch, "E63.oppositeSnap0", {"position": v(209.04, -42.92) * mm});
            skLineSegment(sketch, "E63.top", {"start": v(199.04, -33.95) * mm, "end": v(209.04, -33.95) * mm});
            skLineSegment(sketch, "E63.left", {"start": v(199.04, -37.92) * mm, "end": v(199.04, -33.95) * mm});
            skLineSegment(sketch, "E63.right", {"start": v(209.04, -37.92) * mm, "end": v(209.04, -33.95) * mm});
            skLineSegment(sketch, "E64.top", {"start": v(217.04, -33.95) * mm, "end": v(227.02, -33.95) * mm});
            skLineSegment(sketch, "E64.left", {"start": v(217.04, -37.92) * mm, "end": v(217.04, -33.95) * mm});
            skLineSegment(sketch, "E64.right", {"start": v(227.02, -37.92) * mm, "end": v(227.02, -33.95) * mm});
            skSolve(sketch);
        }
        {
            var Q0;
            Q0=qSketchRegion(id+"F0",true);
            var Q1;
            Q1=makeQuery(id+"F0.imprint","IMPRINT",FACE,{"disambiguationData":[TD([[makeQuery(id+"F0.imprint","IMPRINT",EDGE,{"derivedFrom":sQuery(id+"F0.wireOp",EDGE,"E0")}),-1.0]])]});
            var Q2;
            {var subQ0=sQuery(id+"F0.wireOp",EDGE,"E6.bottom");Q2=makeQuery(id+"F0.imprint","IMPRINT",FACE,{"disambiguationData":[TD([[makeQuery(id+"F0.imprint","IMPRINT",EDGE,{"derivedFrom":subQ0}),1.0]])]});}
            var Q3;
            {var subQ0=sQuery(id+"F0.wireOp",EDGE,"4da5e357-2c40-4844-ab1d-fab356adb77c.3.1");Q3=makeQuery(id+"F0.imprint","IMPRINT",FACE,{"disambiguationData":[TD([[makeQuery(id+"F0.imprint","IMPRINT",EDGE,{"derivedFrom":subQ0}),1.0]])]});}
            var Q4;
            {var subQ0=sQuery(id+"F0.wireOp",EDGE,"4da5e357-2c40-4844-ab1d-fab356adb77c.6.1");Q4=makeQuery(id+"F0.imprint","IMPRINT",FACE,{"disambiguationData":[TD([[makeQuery(id+"F0.imprint","IMPRINT",EDGE,{"derivedFrom":subQ0}),1.0]])]});}
            var Q5;
            Q5=makeQuery(id+"F0.imprint","IMPRINT",FACE,{"disambiguationData":[TD([[makeQuery(id+"F0.imprint","IMPRINT",EDGE,{"derivedFrom":sQuery(id+"F0.wireOp",EDGE,"E1")}),-1.0]])]});
            extrude(context, id + "F1", {"entities" : qUnion([Q0, Q1, Q2, Q3, Q4, Q5]), "depth" : 7 * mm, "offsetDistance" : 25.4 * mm});
        }
    });
